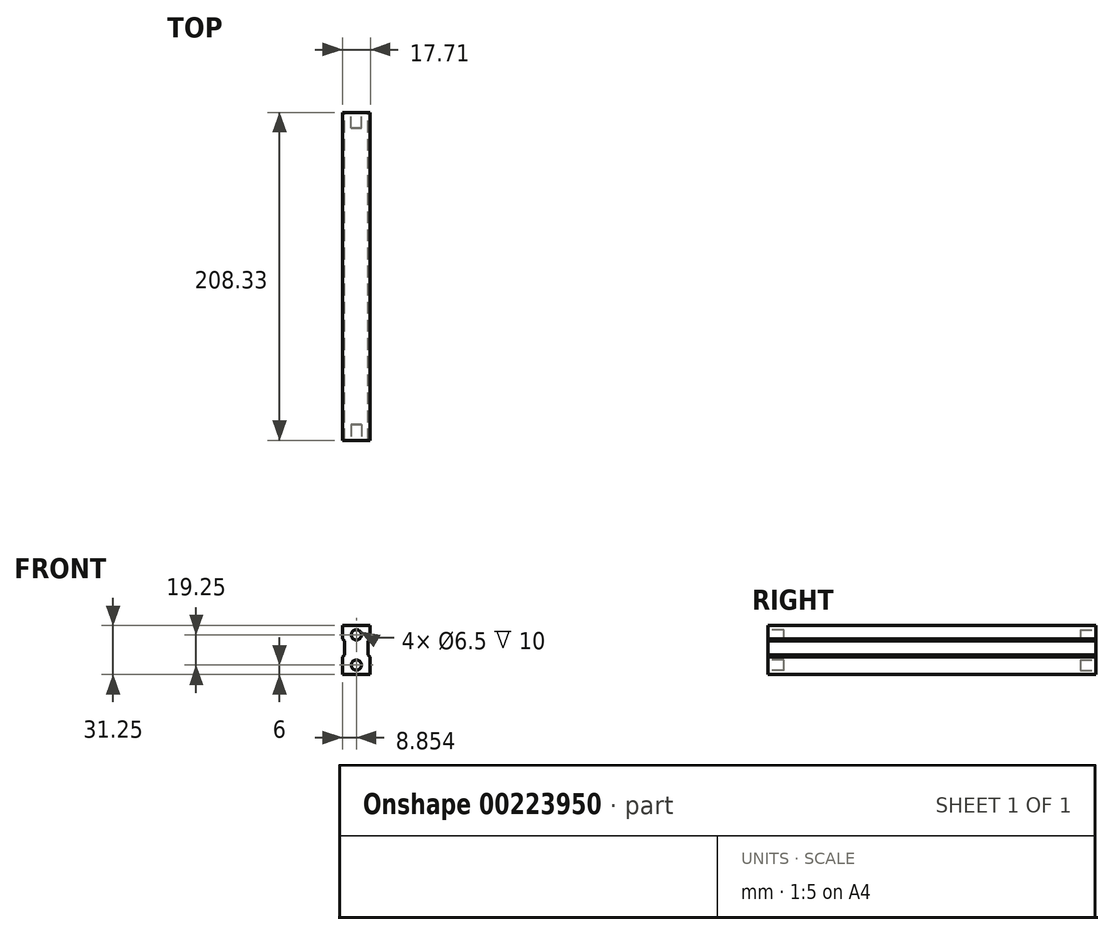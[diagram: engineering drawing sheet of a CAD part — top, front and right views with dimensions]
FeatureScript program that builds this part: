
annotation { "Feature Type Name" : "Feature", "Feature Type Description" : "" }
export const myFeature = defineFeature(function(context is Context, id is Id, definition is map)
    precondition{}
    {
        {
            var Q0;
            Q0=qCreatedBy(makeId("Front.planeOp"),FACE);
            var sketch = newSketch(context, id + "F0", { "sketchPlane" : qUnion([Q0])});
            skLineSegment(sketch, "E0.bottom", {"start": v(0, 0) * mm, "end": v(17.7, 0) * mm, "construction": true});
            skLineSegment(sketch, "E0.top", {"start": v(0, 31.25) * mm, "end": v(17.7, 31.25) * mm, "construction": true});
            skLineSegment(sketch, "E0.left", {"start": v(0, 0) * mm, "end": v(0, 31.25) * mm, "construction": true});
            skLineSegment(sketch, "E0.right", {"start": v(17.7, 0) * mm, "end": v(17.7, 31.25) * mm, "construction": true});
            skLineSegment(sketch, "E1", {"start": v(8.85, 31.25) * mm, "end": v(8.85, 0) * mm, "construction": true});
            skLineSegment(sketch, "E2", {"start": v(8.85, 0) * mm, "end": v(0, 0) * mm});
            skLineSegment(sketch, "E3", {"start": v(0, 11.35) * mm, "end": v(1.35, 12.6) * mm});
            skLineSegment(sketch, "E4", {"start": v(1.35, 12.6) * mm, "end": v(1.35, 21.35) * mm});
            skLineSegment(sketch, "E5", {"start": v(1.35, 21.35) * mm, "end": v(0, 22.6) * mm});
            skLineSegment(sketch, "E6", {"start": v(0, 22.6) * mm, "end": v(0, 31.25) * mm});
            skLineSegment(sketch, "E7", {"start": v(8.85, 31.25) * mm, "end": v(0, 31.25) * mm});
            skLineSegment(sketch, "E8", {"start": v(0, 0) * mm, "end": v(0, 11.35) * mm});
            skLineSegment(sketch, "E9.MirrorCS", {"start": v(16.35, 21.35) * mm, "end": v(17.7, 22.6) * mm});
            skLineSegment(sketch, "E10.MirrorCS", {"start": v(17.7, 11.35) * mm, "end": v(16.35, 12.6) * mm});
            skLineSegment(sketch, "E11.MirrorCS", {"start": v(17.7, 0) * mm, "end": v(17.7, 11.35) * mm});
            skLineSegment(sketch, "E12.MirrorCS", {"start": v(8.85, 31.25) * mm, "end": v(17.7, 31.25) * mm});
            skLineSegment(sketch, "E13.MirrorCS", {"start": v(8.85, 0) * mm, "end": v(17.7, 0) * mm});
            skLineSegment(sketch, "E14.MirrorCS", {"start": v(16.35, 12.6) * mm, "end": v(16.35, 21.35) * mm});
            skLineSegment(sketch, "E15.MirrorCS", {"start": v(17.7, 22.6) * mm, "end": v(17.7, 31.25) * mm});
            skSolve(sketch);
        }
        {
            var Q0;
            Q0=makeQuery(id+"F0.imprint","IMPRINT",FACE,{"disambiguationData":[TD([[makeQuery(id+"F0.imprint","IMPRINT",EDGE,{"derivedFrom":sQuery(id+"F0.wireOp",EDGE,"E2")}),-1.0]])]});
            extrude(context, id + "F1", {"entities" : qUnion([Q0]), "depth" : 10000 / 48 * mm});
        }
        {
            var Q0;
            Q0=makeQuery(id+"F1.opExtrude","CAP_FACE",FACE,{"disambiguationData":[OSD([sQuery(id+"F0.wireOp",EDGE,"E2"),sQuery(id+"F0.wireOp",EDGE,"E3"),sQuery(id+"F0.wireOp",EDGE,"E4"),sQuery(id+"F0.wireOp",EDGE,"E5"),sQuery(id+"F0.wireOp",EDGE,"E6"),sQuery(id+"F0.wireOp",EDGE,"E7"),sQuery(id+"F0.wireOp",EDGE,"E8"),sQuery(id+"F0.wireOp",EDGE,"E9.MirrorCS"),sQuery(id+"F0.wireOp",EDGE,"E10.MirrorCS"),sQuery(id+"F0.wireOp",EDGE,"E11.MirrorCS"),sQuery(id+"F0.wireOp",EDGE,"E12.MirrorCS"),sQuery(id+"F0.wireOp",EDGE,"E13.MirrorCS"),sQuery(id+"F0.wireOp",EDGE,"E14.MirrorCS"),sQuery(id+"F0.wireOp",EDGE,"E15.MirrorCS")])],"isStart":false});
            var sketch = newSketch(context, id + "F2", { "sketchPlane" : qUnion([Q0])});
            skLineSegment(sketch, "E16.bottom", {"start": v(0, 31.25) * mm, "end": v(17.7, 31.25) * mm, "construction": true});
            skLineSegment(sketch, "E16.top", {"start": v(0, 0) * mm, "end": v(17.7, 0) * mm, "construction": true});
            skLineSegment(sketch, "E16.left", {"start": v(0, 31.25) * mm, "end": v(0, 0) * mm, "construction": true});
            skLineSegment(sketch, "E16.right", {"start": v(17.7, 31.25) * mm, "end": v(17.7, 0) * mm, "construction": true});
            skLineSegment(sketch, "E17", {"start": v(8.85, 31.25) * mm, "end": v(8.85, 0) * mm, "construction": true});
            skCircle(sketch, "E18", {"center": v(8.85, 6) * mm, "radius": 3.25 * mm});
            skCircle(sketch, "E19", {"center": v(8.85, 25.25) * mm, "radius": 3.25 * mm});
            skSolve(sketch);
        }
        {
            var Q0;
            Q0 = qSketchRegion(id + "F2", true);
            extrude(context, id + "F3", {"entities" : qUnion([Q0]), "operationType" : NewBodyOperationType.REMOVE, "oppositeDirection" : true, "depth" : 10 * mm});
        }
        {
            var Q0;
            Q0=makeQuery(id+"F1.opExtrude","CAP_FACE",FACE,{"disambiguationData":[OSD([sQuery(id+"F0.wireOp",EDGE,"E2"),sQuery(id+"F0.wireOp",EDGE,"E3"),sQuery(id+"F0.wireOp",EDGE,"E4"),sQuery(id+"F0.wireOp",EDGE,"E5"),sQuery(id+"F0.wireOp",EDGE,"E6"),sQuery(id+"F0.wireOp",EDGE,"E7"),sQuery(id+"F0.wireOp",EDGE,"E8"),sQuery(id+"F0.wireOp",EDGE,"E9.MirrorCS"),sQuery(id+"F0.wireOp",EDGE,"E10.MirrorCS"),sQuery(id+"F0.wireOp",EDGE,"E11.MirrorCS"),sQuery(id+"F0.wireOp",EDGE,"E12.MirrorCS"),sQuery(id+"F0.wireOp",EDGE,"E13.MirrorCS"),sQuery(id+"F0.wireOp",EDGE,"E14.MirrorCS"),sQuery(id+"F0.wireOp",EDGE,"E15.MirrorCS")])],"isStart":true});
            var sketch = newSketch(context, id + "F4", { "sketchPlane" : qUnion([Q0])});
            skLineSegment(sketch, "E20.bottom", {"start": v(-17.7, 31.25) * mm, "end": v(0, 31.25) * mm, "construction": true});
            skLineSegment(sketch, "E20.top", {"start": v(-17.7, 0) * mm, "end": v(0, 0) * mm, "construction": true});
            skLineSegment(sketch, "E20.left", {"start": v(-17.7, 31.25) * mm, "end": v(-17.7, 0) * mm, "construction": true});
            skLineSegment(sketch, "E20.right", {"start": v(0, 31.25) * mm, "end": v(0, 0) * mm, "construction": true});
            skLineSegment(sketch, "E21", {"start": v(-8.85, 31.25) * mm, "end": v(-8.85, 0) * mm, "construction": true});
            skCircle(sketch, "E22", {"center": v(-8.85, 6) * mm, "radius": 3.25 * mm});
            skCircle(sketch, "E23", {"center": v(-8.85, 25.25) * mm, "radius": 3.25 * mm});
            skSolve(sketch);
        }
        {
            var Q0;
            Q0 = qSketchRegion(id + "F4", true);
            extrude(context, id + "F5", {"entities" : qUnion([Q0]), "operationType" : NewBodyOperationType.REMOVE, "oppositeDirection" : true, "depth" : 10 * mm});
        }
    });
